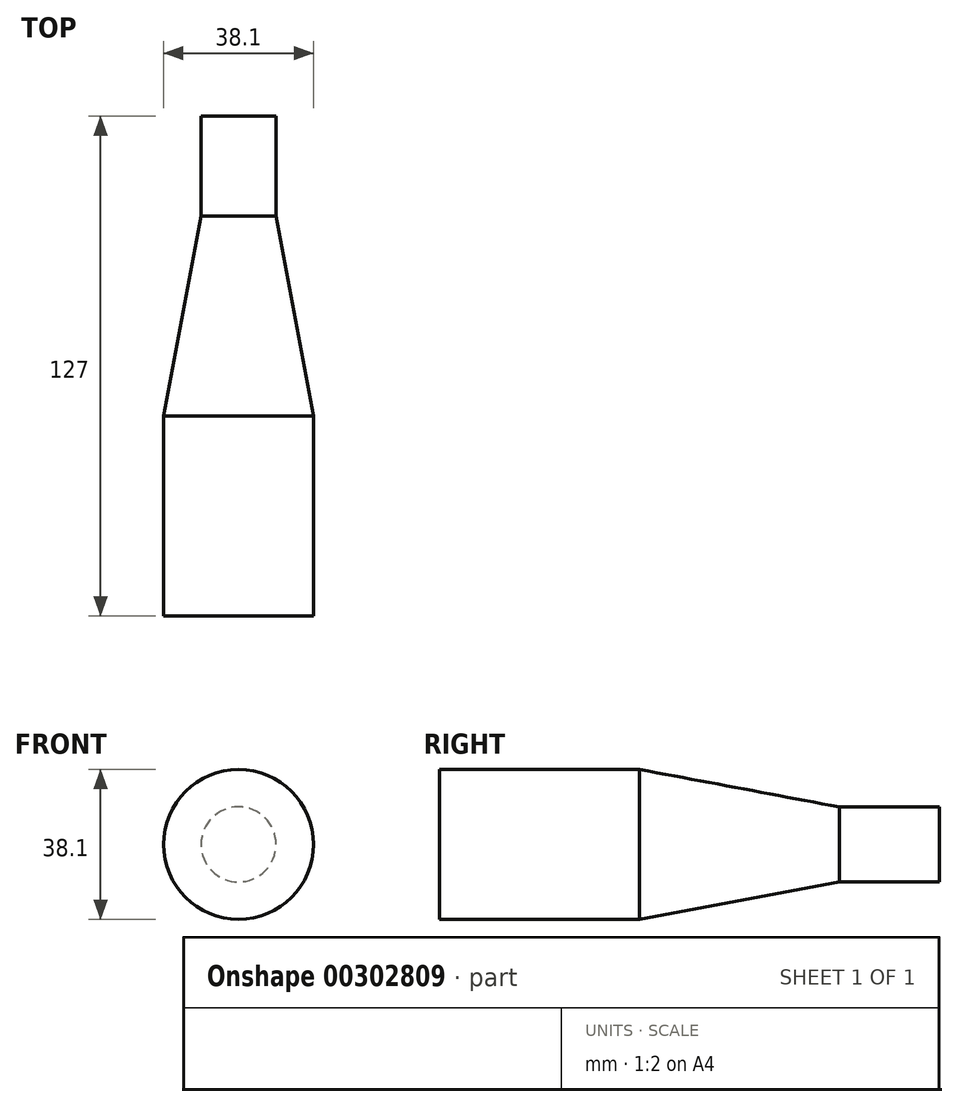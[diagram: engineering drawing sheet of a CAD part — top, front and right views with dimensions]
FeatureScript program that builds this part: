
annotation { "Feature Type Name" : "Feature", "Feature Type Description" : "" }
export const myFeature = defineFeature(function(context is Context, id is Id, definition is map)
    precondition{}
    {
        {
            var Q0;
            Q0=qCreatedBy(makeId("Right.planeOp"),FACE);
            var sketch = newSketch(context, id + "F0", { "sketchPlane" : qUnion([Q0])});
            skLineSegment(sketch, "E0", {"start": v(0, 0) * mm, "end": v(-127, 0) * mm});
            skLineSegment(sketch, "E1", {"start": v(-127, 0) * mm, "end": v(-127, 19.05) * mm});
            skLineSegment(sketch, "E2", {"start": v(-127, 19.05) * mm, "end": v(-76.2, 19.05) * mm});
            skLineSegment(sketch, "E3", {"start": v(-76.2, 19.05) * mm, "end": v(-25.4, 9.52) * mm});
            skLineSegment(sketch, "E4", {"start": v(-25.4, 9.52) * mm, "end": v(0, 9.52) * mm});
            skLineSegment(sketch, "E5", {"start": v(0, 9.52) * mm, "end": v(0, 0) * mm});
            skSolve(sketch);
        }
        {
            var Q0;
            Q0=makeQuery(id+"F0.imprint","IMPRINT",FACE,{"disambiguationData":[TD([[makeQuery(id+"F0.imprint","IMPRINT",EDGE,{"derivedFrom":sQuery(id+"F0.wireOp",EDGE,"E0")}),-1.0]])]});
            var Q1;
            Q1=sQuery(id+"F0.wireOp",EDGE,"E0");
            revolve(context, id + "F1", {"entities" : qUnion([Q0]), "axis" : qUnion([Q1]), "revolveType" : RevolveType.FULL});
        }
    });
